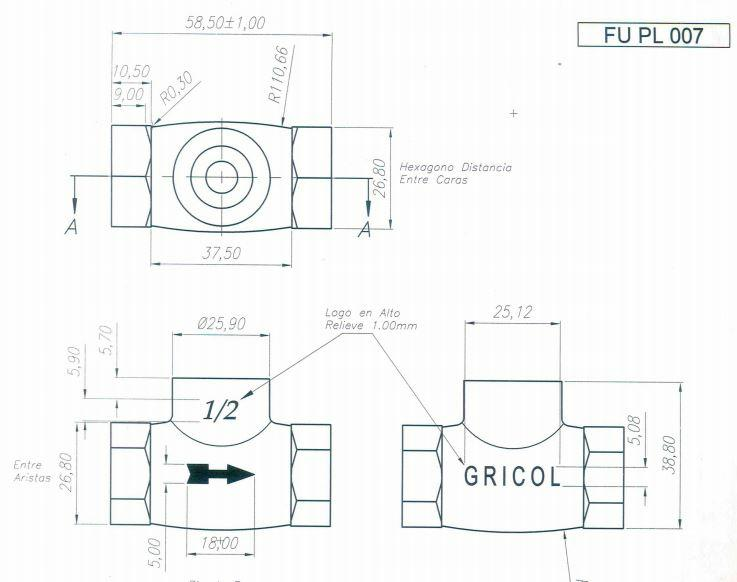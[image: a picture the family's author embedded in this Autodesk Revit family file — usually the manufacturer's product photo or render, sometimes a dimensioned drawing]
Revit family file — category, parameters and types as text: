
# Revit family: 01-9977-11 LLAVE MANGUERA PESADA METAL CROMO
name_source: partatom
category: Aparatos sanitarios
units: mm (PartAtom-declared; Revit-internal decimal feet)

## family parameters
Anfitrión = Cara
Compartido = No
Corte con vacíos al cargar = No
Cota de conector redondo = Diámetro de uso
Número OmniClass = 23.31.11.00
Punto de cálculo de habitación = No
Tipo de pieza = Normal

## types (1)
- 01-9977-11
    Acometida = Dim 1/2" NPT
    Alto = 98 mm  [stored 0.321522 ft]
    Ancho = 102 mm
    Ancho manija llave = 60 mm
    Conexión AC = Sí
    Conexión AF = Sí
    Conexión de residuos = No
    Conexión de ventilación = No
    Descripción = Llave jardin
    Elevación por defecto = 0 mm  [stored 0 ft]
    Fabricante = Gricol
    Imagen de tipo = LLAVE MANGUERA PESADA METAL CROMO.jpg
    Link Ficha Tecnica = http://infotecnica.gricol.com
    Metal Laton Cromado = Metal Laton Cromado
    Metal Zamak Cromado = Metal Zamak Cromado
    Modelo = 01-9977-11
    Product Name = LLAVE MANGUERA PESADA METAL CROMO
    Salida = Dim 3/4" NH
    URL = https://www.gricol.com

note: [stored X ft] marks values corroborated as IEEE doubles in the binary element streams (Revit-internal decimal feet)

## geometry (parser evidence)
native form markers: Blend x4, Sweep x6
no freeform markers — native parametric forms only
